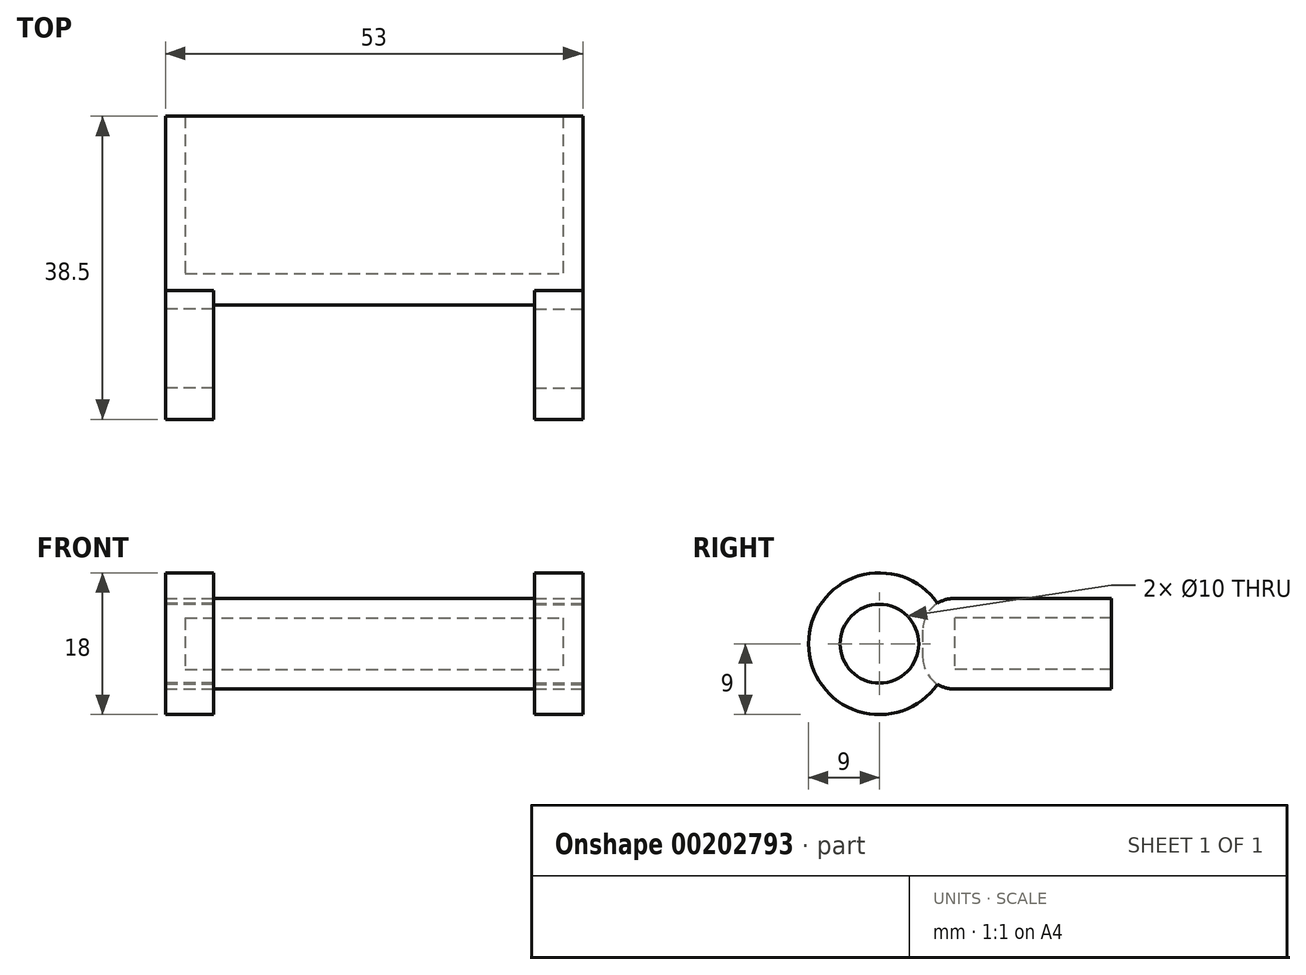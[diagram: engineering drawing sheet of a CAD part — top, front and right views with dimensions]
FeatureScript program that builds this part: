
annotation { "Feature Type Name" : "Feature", "Feature Type Description" : "" }
export const myFeature = defineFeature(function(context is Context, id is Id, definition is map)
    precondition{}
    {
        {
            var Q0;
            Q0=qCreatedBy(makeId("Front.planeOp"),FACE);
            var sketch = newSketch(context, id + "F0", { "sketchPlane" : qUnion([Q0])});
            skLineSegment(sketch, "E0.bottom", {"start": v(-24, 3.25) * mm, "end": v(24, 3.25) * mm});
            skLineSegment(sketch, "E0.top", {"start": v(-24, -3.25) * mm, "end": v(24, -3.25) * mm});
            skLineSegment(sketch, "E0.left", {"start": v(-24, 3.25) * mm, "end": v(-24, -3.25) * mm});
            skLineSegment(sketch, "E0.right", {"start": v(24, 3.25) * mm, "end": v(24, -3.25) * mm});
            skLineSegment(sketch, "E1", {"start": v(0, 3.25) * mm, "end": v(0, -3.25) * mm, "construction": true});
            skLineSegment(sketch, "E2.0", {"start": v(26.5, 5.75) * mm, "end": v(26.5, -5.75) * mm});
            skLineSegment(sketch, "E2.1", {"start": v(-26.5, 5.75) * mm, "end": v(26.5, 5.75) * mm});
            skLineSegment(sketch, "E2.2", {"start": v(-26.5, 5.75) * mm, "end": v(-26.5, -5.75) * mm});
            skLineSegment(sketch, "E2.3", {"start": v(-26.5, -5.75) * mm, "end": v(26.5, -5.75) * mm});
            skSolve(sketch);
        }
        {
            var Q0;
            Q0=makeQuery(id+"F0.imprint","IMPRINT",FACE,{"disambiguationData":[TD([[makeQuery(id+"F0.imprint","IMPRINT",EDGE,{"derivedFrom":sQuery(id+"F0.wireOp",EDGE,"E0.bottom")}),1.0]])]});
            var Q1;
            Q1=makeQuery(id+"F0.imprint","IMPRINT",FACE,{"disambiguationData":[TD([[makeQuery(id+"F0.imprint","IMPRINT",EDGE,{"derivedFrom":sQuery(id+"F0.wireOp",EDGE,"E0.bottom")}),-1.0]])]});
            extrude(context, id + "F1", {"entities" : qUnion([Q0, Q1]), "depth" : 4 * mm});
        }
        {
            var Q0;
            Q0=makeQuery(id+"F0.imprint","IMPRINT",FACE,{"disambiguationData":[TD([[makeQuery(id+"F0.imprint","IMPRINT",EDGE,{"derivedFrom":sQuery(id+"F0.wireOp",EDGE,"E0.bottom")}),1.0]])]});
            extrude(context, id + "F2", {"entities" : qUnion([Q0]), "operationType" : NewBodyOperationType.ADD, "oppositeDirection" : true, "depth" : 20 * mm});
        }
        {
            var Q0;
            {var subQ0=sQuery(id+"F0.wireOp",EDGE,"E2.0");Q0=makeQuery(id+"F2.boolean.opBoolean","MERGE",FACE,{"derivedFrom":[makeQuery(id+"F1.opExtrude","SWEPT_FACE",FACE,{"disambiguationData":[OSD([subQ0])]}),makeQuery(id+"F2.opExtrude","SWEPT_FACE",FACE,{"disambiguationData":[OSD([subQ0])]})]});}
            var sketch = newSketch(context, id + "F3", { "sketchPlane" : qUnion([Q0])});
            skLineSegment(sketch, "E3.bottom", {"start": v(0, 0) * mm, "end": v(-9.5, 0) * mm, "construction": true});
            skLineSegment(sketch, "E3.top", {"start": v(0, -5) * mm, "end": v(-9.5, -5) * mm, "construction": true});
            skLineSegment(sketch, "E3.left", {"start": v(0, 0) * mm, "end": v(0, -5) * mm, "construction": true});
            skLineSegment(sketch, "E3.right", {"start": v(-9.5, 0) * mm, "end": v(-9.5, -5) * mm, "construction": true});
            skCircle(sketch, "E4", {"center": v(-9.5, 0) * mm, "radius": 5 * mm});
            skCircle(sketch, "E5.0", {"center": v(-9.5, 0) * mm, "radius": 9 * mm});
            skSolve(sketch);
        }
        {
            var Q0;
            {var subQ0=sQuery(id+"F0.wireOp",EDGE,"E2.2");Q0=makeQuery(id+"F2.boolean.opBoolean","MERGE",FACE,{"derivedFrom":[makeQuery(id+"F1.opExtrude","SWEPT_FACE",FACE,{"disambiguationData":[OSD([subQ0])]}),makeQuery(id+"F2.opExtrude","SWEPT_FACE",FACE,{"disambiguationData":[OSD([subQ0])]})]});}
            var sketch = newSketch(context, id + "F4", { "sketchPlane" : qUnion([Q0])});
            skCircle(sketch, "E6", {"center": v(9.5, 0) * mm, "radius": 5 * mm});
            skCircle(sketch, "E7", {"center": v(9.5, 0) * mm, "radius": 9 * mm});
            skSolve(sketch);
        }
        {
            var Q0;
            Q0=makeQuery(id+"F4.imprint","IMPRINT",FACE,{"disambiguationData":[TD([[makeQuery(id+"F4.imprint","IMPRINT",EDGE,{"derivedFrom":sQuery(id+"F4.wireOp",EDGE,"E6")}),-1.0]])]});
            extrude(context, id + "F5", {"entities" : qUnion([Q0]), "operationType" : NewBodyOperationType.ADD, "oppositeDirection" : true, "depth" : 6.1 * mm});
        }
        {
            var Q0;
            Q0=makeQuery(id+"F3.imprint","IMPRINT",FACE,{"disambiguationData":[TD([[makeQuery(id+"F3.imprint","IMPRINT",EDGE,{"derivedFrom":sQuery(id+"F3.wireOp",EDGE,"E4")}),-1.0]])]});
            extrude(context, id + "F6", {"entities" : qUnion([Q0]), "operationType" : NewBodyOperationType.ADD, "oppositeDirection" : true, "depth" : 6.1 * mm});
        }
        {
            var Q0;
            Q0=makeQuery(id+"F1.opExtrude","CAP_EDGE",EDGE,{"disambiguationData":[OSD([sQuery(id+"F0.wireOp",EDGE,"E2.1")])],"isStart":false});
            var Q1;
            Q1=makeQuery(id+"F1.opExtrude","CAP_EDGE",EDGE,{"disambiguationData":[OSD([sQuery(id+"F0.wireOp",EDGE,"E2.3")])],"isStart":false});
            fillet(context, id + "F7", {"entities" : qUnion([Q0, Q1]), "radius" : 4 * mm, "tangentPropagation" : true, "allowEdgeOverflow" : false});
        }
    });
